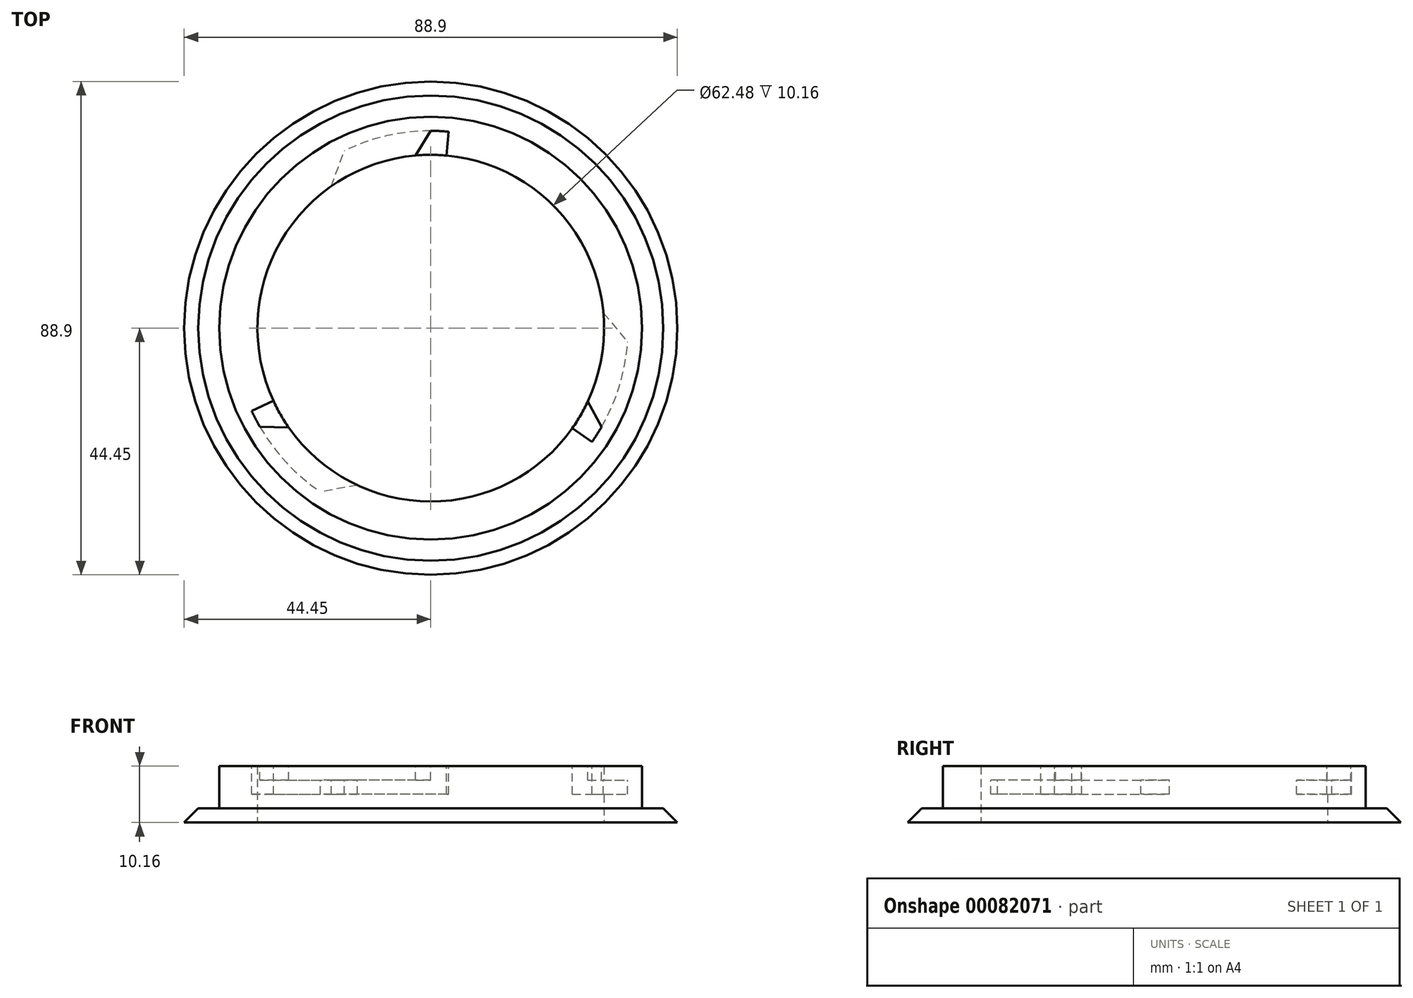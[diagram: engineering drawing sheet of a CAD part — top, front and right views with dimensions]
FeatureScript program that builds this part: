
annotation { "Feature Type Name" : "Feature", "Feature Type Description" : "" }
export const myFeature = defineFeature(function(context is Context, id is Id, definition is map)
    precondition{}
    {
        {
            var Q0;
            Q0=qCreatedBy(makeId("Top.planeOp"),FACE);
            var sketch = newSketch(context, id + "F0", { "sketchPlane" : qUnion([Q0])});
            skCircle(sketch, "E0", {"center": v(0, 0) * mm, "radius": 44.45 * mm});
            skCircle(sketch, "E1", {"center": v(0, 0) * mm, "radius": 31.24 * mm});
            skSolve(sketch);
        }
        {
            var Q0;
            Q0 = qSketchRegion(id + "F0", true);
            extrude(context, id + "F1", {"entities" : qUnion([Q0]), "depth" : 2.54 * mm});
        }
        {
            var Q0;
            Q0=makeQuery(id+"F1.opExtrude","CAP_FACE",FACE,{"disambiguationData":[OSD([sQuery(id+"F0.wireOp",EDGE,"E0"),sQuery(id+"F0.wireOp",EDGE,"E1")])],"isStart":false});
            var sketch = newSketch(context, id + "F2", { "sketchPlane" : qUnion([Q0])});
            skCircle(sketch, "E2.0.0", {"center": v(0, 0) * mm, "radius": 44.45 * mm});
            skCircle(sketch, "E3", {"center": v(0, 0) * mm, "radius": 38.1 * mm});
            skCircle(sketch, "E4", {"center": v(0, 0) * mm, "radius": 31.24 * mm});
            skSolve(sketch);
        }
        {
            var Q0;
            Q0=makeQuery(id+"F2.imprint","IMPRINT",FACE,{"disambiguationData":[TD([[makeQuery(id+"F2.imprint","IMPRINT",EDGE,{"derivedFrom":sQuery(id+"F2.wireOp",EDGE,"E3")}),1.0]])]});
            extrude(context, id + "F3", {"entities" : qUnion([Q0]), "operationType" : NewBodyOperationType.ADD, "depth" : 5.08 * mm});
        }
        {
            var Q0;
            Q0=makeQuery(id+"F3.opExtrude","CAP_FACE",FACE,{"disambiguationData":[OSD([sQuery(id+"F2.wireOp",EDGE,"E3"),sQuery(id+"F2.wireOp",EDGE,"E4")])],"isStart":false});
            var sketch = newSketch(context, id + "F4", { "sketchPlane" : qUnion([Q0])});
            skCircle(sketch, "E5", {"center": v(0, 0) * mm, "radius": 28.7 * mm});
            skArc(sketch, "E6", {"start": v(-2.72, 31.12) * mm, "mid": v(-27.03, 15.67) * mm, "end": v(-28.36, -13.1) * mm});
            skArc(sketch, "E7", {"start": v(-32.28, -14.92) * mm, "mid": v(-31.57, -16.36) * mm, "end": v(-30.8, -17.78) * mm});
            skLineSegment(sketch, "E8", {"start": v(0, 0) * mm, "end": v(0, 35.56) * mm, "construction": true});
            skLineSegment(sketch, "E9", {"start": v(0, 0) * mm, "end": v(30.8, -17.78) * mm, "construction": true});
            skLineSegment(sketch, "E10", {"start": v(0, 0) * mm, "end": v(-30.8, -17.78) * mm, "construction": true});
            skLineSegment(sketch, "E11", {"start": v(2.83, 31.11) * mm, "end": v(3.22, 35.41) * mm});
            skLineSegment(sketch, "E12", {"start": v(25.53, -18) * mm, "end": v(29.06, -20.5) * mm});
            skLineSegment(sketch, "E13", {"start": v(-28.36, -13.1) * mm, "end": v(-32.28, -14.92) * mm});
            skArc(sketch, "E14.trimOffspring", {"start": v(29.06, -20.5) * mm, "mid": v(29.96, -19.16) * mm, "end": v(30.8, -17.78) * mm});
            skArc(sketch, "E15.trimOffspring", {"start": v(3.22, 35.41) * mm, "mid": v(1.61, 35.52) * mm, "end": v(0, 35.56) * mm});
            skArc(sketch, "E16.trimOffspring", {"start": v(-25.6, -17.92) * mm, "mid": v(27.03, -15.67) * mm, "end": v(2.83, 31.11) * mm});
            skCircle(sketch, "E17", {"center": v(0, 0) * mm, "radius": 35.56 * mm, "construction": true});
            skLineSegment(sketch, "E18", {"start": v(0, 0) * mm, "end": v(-15.03, -32.23) * mm, "construction": true});
            skLineSegment(sketch, "E19", {"start": v(0, 0) * mm, "end": v(35.42, 3.1) * mm, "construction": true});
            skLineSegment(sketch, "E20", {"start": v(0, 0) * mm, "end": v(-20.4, 29.13) * mm, "construction": true});
            skArc(sketch, "E21", {"start": v(-32.28, -14.92) * mm, "mid": v(-27.07, -23.05) * mm, "end": v(-19.87, -29.5) * mm});
            skArc(sketch, "E22.trimOffspring", {"start": v(3.22, 35.41) * mm, "mid": v(-6.43, 34.97) * mm, "end": v(-15.6, 31.95) * mm});
            skArc(sketch, "E23.trimOffspring", {"start": v(29.06, -20.5) * mm, "mid": v(33.5, -11.92) * mm, "end": v(35.47, -2.46) * mm});
            skLineSegment(sketch, "E24", {"start": v(-17.92, 25.6) * mm, "end": v(-15.6, 31.95) * mm});
            skLineSegment(sketch, "E25", {"start": v(-13.2, -28.31) * mm, "end": v(-19.87, -29.5) * mm});
            skLineSegment(sketch, "E26", {"start": v(31.12, 2.72) * mm, "end": v(35.47, -2.46) * mm});
            skSolve(sketch);
        }
        {
            var Q0;
            {var subQ3=sQuery(id+"F4.wireOp",EDGE,"E13");Q0=makeQuery(id+"F4.imprint","IMPRINT",FACE,{"disambiguationData":[TD([[makeQuery(id+"F4.imprint","IMPRINT",EDGE,{"derivedFrom":subQ3}),1.0]])]});}
            var Q1;
            {var subQ3=sQuery(id+"F4.wireOp",EDGE,"E11");Q1=makeQuery(id+"F4.imprint","IMPRINT",FACE,{"disambiguationData":[TD([[makeQuery(id+"F4.imprint","IMPRINT",EDGE,{"derivedFrom":subQ3}),1.0]])]});}
            var Q2;
            {var subQ1=sQuery(id+"F4.wireOp",EDGE,"E12");Q2=makeQuery(id+"F4.imprint","IMPRINT",FACE,{"disambiguationData":[TD([[makeQuery(id+"F4.imprint","IMPRINT",EDGE,{"derivedFrom":subQ1}),1.0]])]});}
            extrude(context, id + "F5", {"entities" : qUnion([Q0, Q1, Q2]), "operationType" : NewBodyOperationType.REMOVE, "oppositeDirection" : true, "depth" : 2.54 * mm});
        }
        {
            var Q0;
            Q0=makeQuery(id+"F3.opExtrude","CAP_FACE",FACE,{"disambiguationData":[OSD([sQuery(id+"F2.wireOp",EDGE,"E3"),sQuery(id+"F2.wireOp",EDGE,"E4")])],"isStart":false});
            var sketch = newSketch(context, id + "F6", { "sketchPlane" : qUnion([Q0])});
            skCircle(sketch, "E27", {"center": v(0, 0) * mm, "radius": 31.24 * mm});
            skCircle(sketch, "E28.0.0", {"center": v(0, 0) * mm, "radius": 38.1 * mm});
            skSolve(sketch);
        }
        {
            var Q0;
            Q0 = qSketchRegion(id + "F6", true);
            extrude(context, id + "F7", {"entities" : qUnion([Q0]), "operationType" : NewBodyOperationType.ADD, "depth" : 2.54 * mm});
        }
        {
            var Q0;
            Q0=makeQuery(id+"F7.opExtrude","CAP_FACE",FACE,{"disambiguationData":[OSD([sQuery(id+"F6.wireOp",EDGE,"E27"),sQuery(id+"F6.wireOp",EDGE,"E28.0.0")])],"isStart":false});
            var sketch = newSketch(context, id + "F8", { "sketchPlane" : qUnion([Q0])});
            skCircle(sketch, "E29", {"center": v(0, 0) * mm, "radius": 28.58 * mm});
            skArc(sketch, "E30", {"start": v(-2.72, 31.12) * mm, "mid": v(-27.03, 15.67) * mm, "end": v(-28.36, -13.1) * mm});
            skArc(sketch, "E31", {"start": v(-32.28, -14.92) * mm, "mid": v(-31.57, -16.36) * mm, "end": v(-30.8, -17.78) * mm});
            skLineSegment(sketch, "E32", {"start": v(0, 0) * mm, "end": v(0, 35.56) * mm, "construction": true});
            skLineSegment(sketch, "E33", {"start": v(0, 0) * mm, "end": v(30.8, -17.78) * mm, "construction": true});
            skLineSegment(sketch, "E34", {"start": v(0, 0) * mm, "end": v(-30.8, -17.78) * mm, "construction": true});
            skLineSegment(sketch, "E35", {"start": v(2.83, 31.11) * mm, "end": v(3.22, 35.41) * mm});
            skLineSegment(sketch, "E36", {"start": v(25.53, -18) * mm, "end": v(29.06, -20.5) * mm});
            skLineSegment(sketch, "E37", {"start": v(-28.36, -13.1) * mm, "end": v(-32.28, -14.92) * mm});
            skArc(sketch, "E38.trimOffspring", {"start": v(29.06, -20.5) * mm, "mid": v(29.96, -19.16) * mm, "end": v(30.8, -17.78) * mm});
            skArc(sketch, "E39.trimOffspring", {"start": v(3.22, 35.41) * mm, "mid": v(1.61, 35.52) * mm, "end": v(0, 35.56) * mm});
            skArc(sketch, "E40.trimOffspring", {"start": v(-25.6, -17.92) * mm, "mid": v(27.03, -15.67) * mm, "end": v(2.83, 31.11) * mm});
            skLineSegment(sketch, "E41", {"start": v(-2.72, 31.12) * mm, "end": v(0, 35.56) * mm});
            skLineSegment(sketch, "E42", {"start": v(28.31, -13.2) * mm, "end": v(30.8, -17.78) * mm});
            skLineSegment(sketch, "E43", {"start": v(-25.6, -17.92) * mm, "end": v(-30.8, -17.78) * mm});
            skSolve(sketch);
        }
        {
            var Q0;
            Q0=makeQuery(id+"F8.imprint","IMPRINT",FACE,{"disambiguationData":[TD([[makeQuery(id+"F8.imprint","IMPRINT",EDGE,{"derivedFrom":sQuery(id+"F8.wireOp",EDGE,"E31")}),1.0]])]});
            var Q1;
            {var subQ0=sQuery(id+"F8.wireOp",EDGE,"E36");Q1=makeQuery(id+"F8.imprint","IMPRINT",FACE,{"disambiguationData":[TD([[makeQuery(id+"F8.imprint","IMPRINT",EDGE,{"derivedFrom":subQ0}),1.0]])]});}
            var Q2;
            {var subQ0=sQuery(id+"F8.wireOp",EDGE,"E35");Q2=makeQuery(id+"F8.imprint","IMPRINT",FACE,{"disambiguationData":[TD([[makeQuery(id+"F8.imprint","IMPRINT",EDGE,{"derivedFrom":subQ0}),1.0]])]});}
            extrude(context, id + "F9", {"entities" : qUnion([Q0, Q1, Q2]), "operationType" : NewBodyOperationType.REMOVE, "oppositeDirection" : true, "depth" : 2.54 * mm});
        }
        {
            var Q0;
            Q0=makeQuery(id+"F1.opExtrude","CAP_EDGE",EDGE,{"disambiguationData":[OSD([sQuery(id+"F0.wireOp",EDGE,"E0")])],"isStart":false});
            chamfer(context, id + "F10", {"entities" : qUnion([Q0]), "width" : 2.54 * mm, "tangentPropagation" : true});
        }
    });
